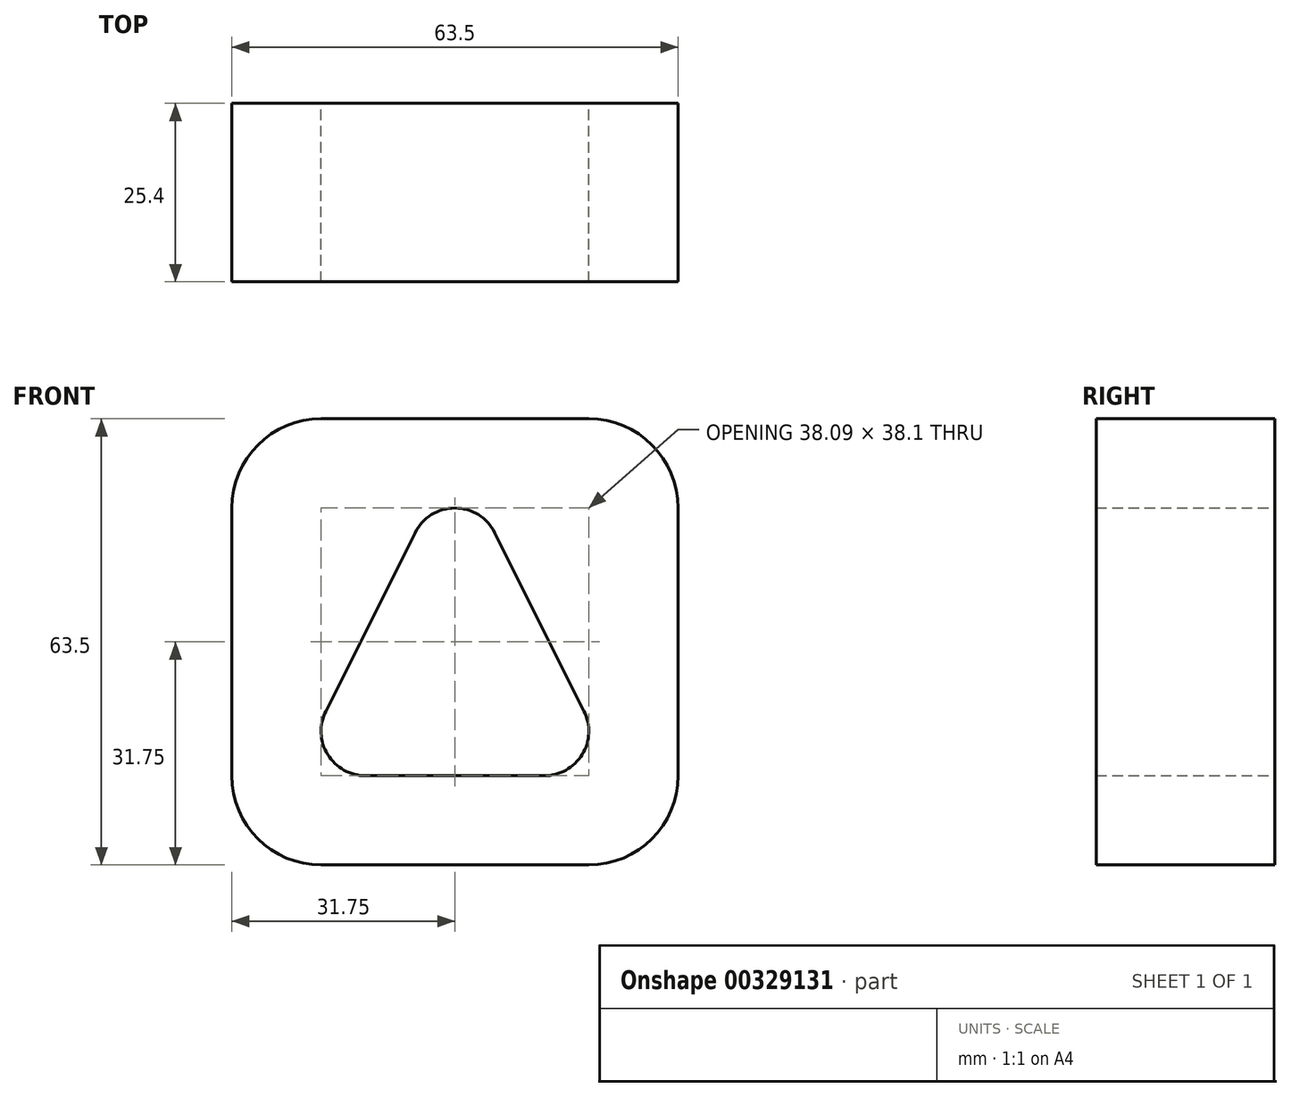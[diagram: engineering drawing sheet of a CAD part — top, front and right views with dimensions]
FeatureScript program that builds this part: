
annotation { "Feature Type Name" : "Feature", "Feature Type Description" : "" }
export const myFeature = defineFeature(function(context is Context, id is Id, definition is map)
    precondition{}
    {
        {
            var Q0;
            Q0=qCreatedBy(makeId("Front.planeOp"),FACE);
            var sketch = newSketch(context, id + "F0", { "sketchPlane" : qUnion([Q0])});
            skLineSegment(sketch, "E0.bottom", {"start": v(0, 0) * mm, "end": v(63.5, 0) * mm});
            skLineSegment(sketch, "E0.top", {"start": v(0, 63.5) * mm, "end": v(63.5, 63.5) * mm});
            skLineSegment(sketch, "E0.left", {"start": v(0, 0) * mm, "end": v(0, 63.5) * mm});
            skLineSegment(sketch, "E0.right", {"start": v(63.5, 0) * mm, "end": v(63.5, 63.5) * mm});
            skArc(sketch, "E1", {"start": v(13.37, 21.89) * mm, "mid": v(13.65, 15.71) * mm, "end": v(19.05, 12.7) * mm});
            skArc(sketch, "E2", {"start": v(37.43, 47.29) * mm, "mid": v(31.75, 50.8) * mm, "end": v(26.07, 47.29) * mm});
            skArc(sketch, "E3", {"start": v(44.45, 12.7) * mm, "mid": v(49.85, 15.71) * mm, "end": v(50.13, 21.89) * mm});
            skLineSegment(sketch, "E4", {"start": v(37.43, 47.29) * mm, "end": v(50.13, 21.89) * mm});
            skLineSegment(sketch, "E5", {"start": v(44.45, 12.7) * mm, "end": v(19.05, 12.7) * mm});
            skLineSegment(sketch, "E6", {"start": v(13.37, 21.89) * mm, "end": v(26.07, 47.29) * mm});
            skSolve(sketch);
        }
        {
            var Q0;
            Q0=makeQuery(id+"F0.imprint","IMPRINT",FACE,{"disambiguationData":[TD([[makeQuery(id+"F0.imprint","IMPRINT",EDGE,{"derivedFrom":sQuery(id+"F0.wireOp",EDGE,"E0.bottom")}),1.0]])]});
            extrude(context, id + "F1", {"entities" : qUnion([Q0]), "depth" : 25.4 * mm});
        }
        {
            var Q0;
            Q0=makeQuery(id+"F1.opExtrude","SWEPT_EDGE",EDGE,{"disambiguationData":[OSD([sQuery(id+"F0.wireOp",EDGE,"E0.top"),sQuery(id+"F0.wireOp",EDGE,"E0.right")])]});
            var Q1;
            Q1=makeQuery(id+"F1.opExtrude","SWEPT_EDGE",EDGE,{"disambiguationData":[OSD([sQuery(id+"F0.wireOp",EDGE,"E0.top"),sQuery(id+"F0.wireOp",EDGE,"E0.left")])]});
            var Q2;
            Q2=makeQuery(id+"F1.opExtrude","SWEPT_EDGE",EDGE,{"disambiguationData":[OSD([sQuery(id+"F0.wireOp",EDGE,"E0.bottom"),sQuery(id+"F0.wireOp",EDGE,"E0.left")])]});
            var Q3;
            Q3=makeQuery(id+"F1.opExtrude","SWEPT_EDGE",EDGE,{"disambiguationData":[OSD([sQuery(id+"F0.wireOp",EDGE,"E0.bottom"),sQuery(id+"F0.wireOp",EDGE,"E0.right")])]});
            fillet(context, id + "F2", {"entities" : qUnion([Q0, Q1, Q2, Q3]), "radius" : 12.7 * mm, "tangentPropagation" : true, "allowEdgeOverflow" : false});
        }
    });
